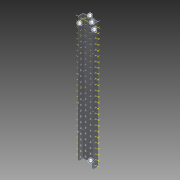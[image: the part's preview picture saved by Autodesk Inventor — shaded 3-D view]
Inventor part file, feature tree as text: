
AUTODESK INVENTOR PART (.ipt)
format: ipt  version: 2015 SP1 (Build 190203100, 203)  size: 2,198,016 bytes
history: native  units: in
note: dims shown in document units (in); Inventor stores cm internally (conversion verified against a paired STEP export)
features: other x131, pattern_linear x2, sheet_metal_op x1, extrude x1, imported_body x1, sketch x1
ambient origin geometry x8: Origin, YZ Plane, XZ Plane, XY Plane, X Axis, Y Axis, Z Axis, Center Point
bodies: Body1 (feature_tree)
feature tree (137):
  sheet_metal_op  "Fold1"
  other  "C-Channel"
  extrude  "length cut"  Depth=1.1811in
  other  "Work Point1"
  other  "Work Point2"
  other  "Work Point3"
  other  "top axis"
  other  "front axis"
  other  "back axis"
  pattern_linear  "top axes"  Count1=25  [1 undecoded]
  pattern_linear  "horiz axes"  Spacing1=0.5in  [1 undecoded]
  other  "Left Plane"
  other  "Right Plane"
  imported_body  "Base1"
  sketch  "Sketch1"  dims[d1=0.0in d2=1.1811in d4=0.5in d5=9.8425in d7=0.5in d8=9.8425in d10=0.5in d12=-12.5in d17=0.0in d18=0.0in d19=0.0in d20=0.0in d21=0.0in]
  other  "Work Axis4"
  other  "Work Axis5"
  other  "Work Axis6"
  other  "Work Axis7"
  other  "Work Axis8"
  other  "Work Axis9"
  other  "Work Axis10"
  other  "Work Axis11"
  other  "Work Axis12"
  other  "Work Axis13"
  other  "Work Axis14"
  other  "Work Axis15"
  other  "Work Axis16"
  other  "Work Axis17"
  other  "Work Axis18"
  other  "Work Axis19"
  other  "Work Axis20"
  other  "Work Axis21"
  other  "Work Axis22"
  other  "Work Axis23"
  other  "Work Axis24"
  other  "Work Axis25"
  other  "Work Axis26"
  other  "Work Axis27"
  other  "Work Axis28"
  other  "Work Axis29"
  other  "Work Axis30"
  other  "Work Axis31"
  other  "Work Axis32"
  other  "Work Axis33"
  other  "Work Axis34"
  other  "Work Axis35"
  other  "Work Axis36"
  other  "Work Axis37"
  other  "Work Axis38"
  other  "Work Axis39"
  other  "Work Axis40"
  other  "Work Axis41"
  other  "Work Axis42"
  other  "Work Axis43"
  other  "Work Axis44"
  other  "Work Axis45"
  other  "Work Axis46"
  other  "Work Axis47"
  other  "Work Axis48"
  other  "Work Axis49"
  other  "Work Axis50"
  other  "Work Axis51"
  other  "Work Axis52"
  other  "Work Axis53"
  other  "Work Axis54"
  other  "Work Axis55"
  other  "Work Axis56"
  other  "Work Axis57"
  other  "Work Axis58"
  other  "Work Axis59"
  other  "Work Axis60"
  other  "Work Axis61"
  other  "Work Axis62"
  other  "Work Axis63"
  other  "Work Axis64"
  other  "Work Axis65"
  other  "Work Axis66"
  other  "Work Axis67"
  other  "Work Axis68"
  other  "Work Axis69"
  other  "Work Axis70"
  other  "Work Axis71"
  other  "Work Axis72"
  other  "Work Axis73"
  other  "Work Axis74"
  other  "Work Axis75"
  other  "Work Axis76"
  other  "Work Axis77"
  other  "Work Axis78"
  other  "Work Axis79"
  other  "Work Axis80"
  other  "Work Axis81"
  other  "Work Axis82"
  other  "Work Axis83"
  other  "Work Axis84"
  other  "Work Axis85"
  other  "Work Axis86"
  other  "Work Axis87"
  other  "Work Axis88"
  other  "Work Axis89"
  other  "Work Axis90"
  other  "Work Axis91"
  other  "Work Axis92"
  other  "Work Axis93"
  other  "Work Axis94"
  other  "Work Axis95"
  other  "Work Axis96"
  other  "Work Axis97"
  other  "Work Axis98"
  other  "Work Axis99"
  other  "Work Axis100"
  other  "Work Axis101"
  other  "Work Axis102"
  other  "Work Axis103"
  other  "Work Axis104"
  other  "Work Axis105"
  other  "Work Axis106"
  other  "Work Axis107"
  other  "Work Axis108"
  other  "Work Axis109"
  other  "Work Axis110"
  other  "Work Axis111"
  other  "Work Axis112"
  other  "Work Axis113"
  other  "Work Axis114"
  other  "Work Axis115"
  other  "Work Axis116"
  other  "Work Axis117"
  other  "Work Axis118"
  other  "Work Axis119"
  other  "Work Axis120"
  other  "Work Axis121"
  other  "Work Axis122"
  other  "Work Axis123"
  other  "Work Axis124"
  other  "Work Axis125"
note: 2 required parameter values undecoded (feature->parameter linkage not recoverable at this tier; creation-order binding heuristic only, values carry confidence <= 0.55)
